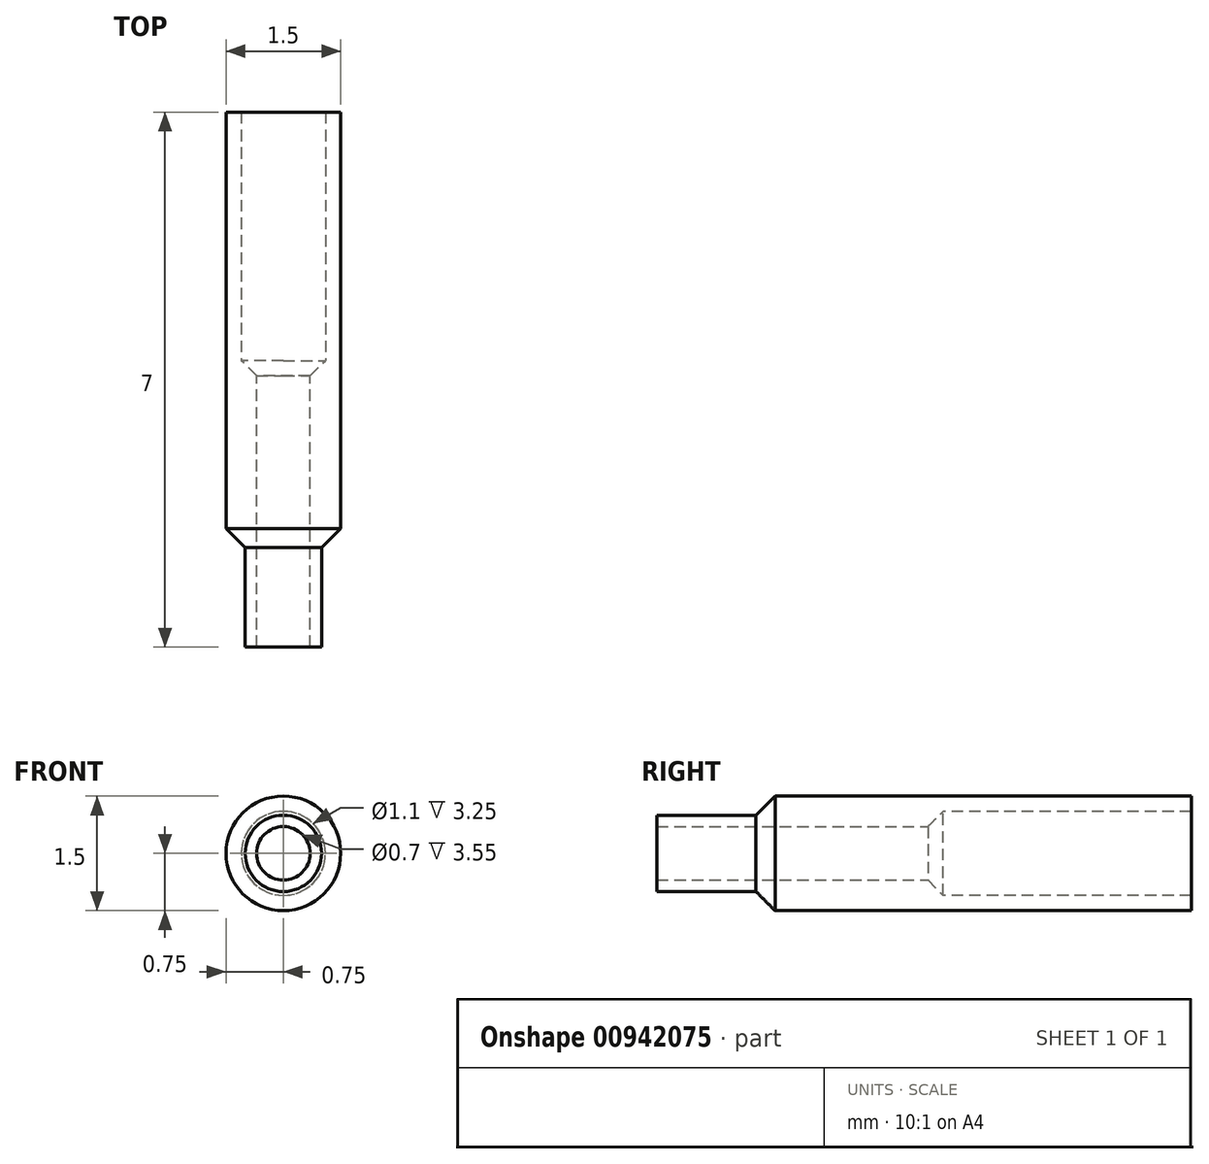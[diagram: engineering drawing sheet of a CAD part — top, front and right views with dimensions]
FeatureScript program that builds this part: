
annotation { "Feature Type Name" : "Feature", "Feature Type Description" : "" }
export const myFeature = defineFeature(function(context is Context, id is Id, definition is map)
    precondition{}
    {
        {
            var Q0;
            Q0=qCreatedBy(makeId("Front.planeOp"),FACE);
            var sketch = newSketch(context, id + "F0", { "sketchPlane" : qUnion([Q0])});
            skCircle(sketch, "E0", {"center": v(0, 0) * mm, "radius": 0.75 * mm});
            skSolve(sketch);
        }
        {
            var Q0;
            Q0=qSketchRegion(id+"F0",true);
            extrude(context, id + "F1", {"entities" : qUnion([Q0]), "depth" : 2.2 * mm, "offsetDistance" : 25 * mm});
        }
        {
            var Q0;
            Q0=makeQuery(id+"F1.opExtrude","CAP_FACE",FACE,{"disambiguationData":[OSD([sQuery(id+"F0.wireOp",EDGE,"E0")])],"isStart":true});
            extrude(context, id + "F2", {"entities" : qUnion([Q0]), "operationType" : NewBodyOperationType.ADD, "depth" : 3.5 * mm, "offsetDistance" : 25 * mm});
        }
        {
            var Q0;
            Q0=qCreatedBy(makeId("Front.planeOp"),FACE);
            var sketch = newSketch(context, id + "F3", { "sketchPlane" : qUnion([Q0])});
            skCircle(sketch, "E1", {"center": v(0, 0) * mm, "radius": 0.55 * mm});
            skSolve(sketch);
        }
        {
            var Q0;
            Q0=qSketchRegion(id+"F3",true);
            extrude(context, id + "F4", {"entities" : qUnion([Q0]), "operationType" : NewBodyOperationType.REMOVE, "oppositeDirection" : true, "depth" : 5 * mm, "offsetDistance" : 25 * mm});
        }
        {
            var Q0;
            Q0=qCreatedBy(makeId("Front.planeOp"),FACE);
            var sketch = newSketch(context, id + "F5", { "sketchPlane" : qUnion([Q0])});
            skCircle(sketch, "E2", {"center": v(0, 0) * mm, "radius": 0.35 * mm});
            skSolve(sketch);
        }
        {
            var Q0;
            Q0=qSketchRegion(id+"F5",true);
            extrude(context, id + "F6", {"entities" : qUnion([Q0]), "operationType" : NewBodyOperationType.REMOVE, "depth" : 5 * mm, "offsetDistance" : 25 * mm});
        }
        {
            var Q0;
            Q0=makeQuery(id+"F4.boolean.opBoolean","COPY",EDGE,{"derivedFrom":makeQuery(id+"F4.opExtrude","CAP_EDGE",EDGE,{"disambiguationData":[OSD([sQuery(id+"F3.wireOp",EDGE,"E1")])],"isStart":true})});
            chamfer(context, id + "F7", {"entities" : qUnion([Q0]), "chamferType" : ChamferType.OFFSET_ANGLE, "width" : 0.25 * mm, "oppositeDirection" : false, "angle" : 45 * degree, "tangentPropagation" : true});
        }
        {
            var Q0;
            Q0=makeQuery(id+"F1.opExtrude","CAP_FACE",FACE,{"disambiguationData":[OSD([sQuery(id+"F0.wireOp",EDGE,"E0")])],"isStart":false});
            var sketch = newSketch(context, id + "F8", { "sketchPlane" : qUnion([Q0])});
            skCircle(sketch, "E3", {"center": v(0, 0) * mm, "radius": 0.5 * mm});
            skSolve(sketch);
        }
        {
            var Q0;
            Q0=makeQuery(id+"F8.imprint","IMPRINT",FACE,{"disambiguationData":[TD([[makeQuery(id+"F8.imprint","IMPRINT",EDGE,{"derivedFrom":sQuery(id+"F8.wireOp",EDGE,"E3")}),1.0]])]});
            extrude(context, id + "F9", {"entities" : qUnion([Q0]), "operationType" : NewBodyOperationType.ADD, "depth" : 1.3 * mm, "offsetDistance" : 25 * mm});
        }
        {
            var Q0;
            Q0=makeQuery(id+"F1.opExtrude","CAP_EDGE",EDGE,{"disambiguationData":[OSD([sQuery(id+"F0.wireOp",EDGE,"E0")])],"isStart":false});
            chamfer(context, id + "F10", {"entities" : qUnion([Q0]), "width" : .25 * mm, "tangentPropagation" : true});
        }
    });
